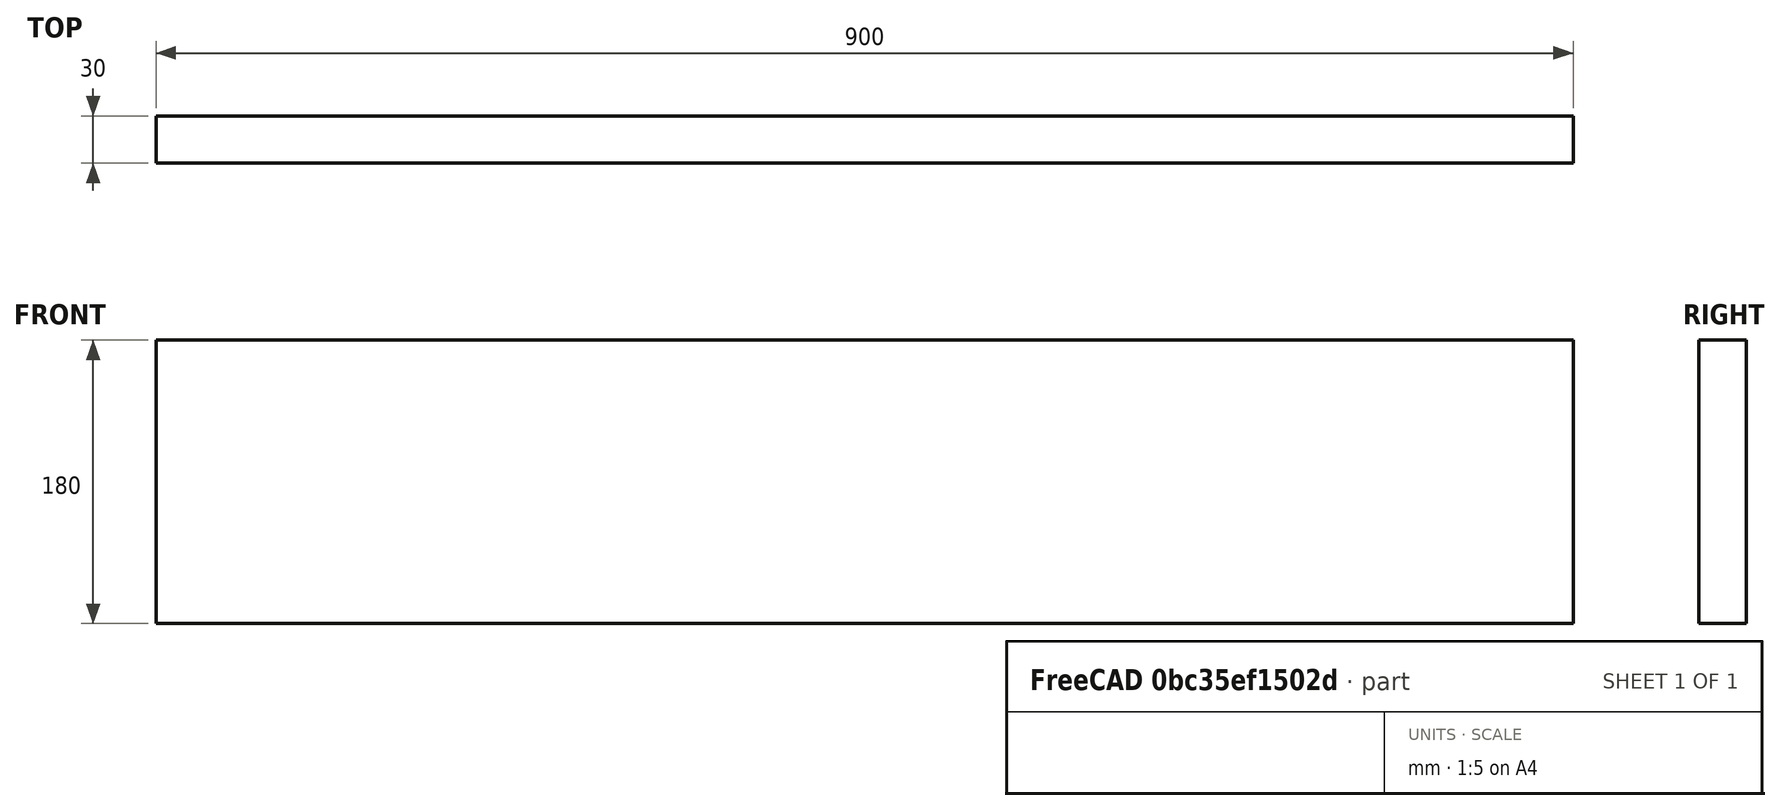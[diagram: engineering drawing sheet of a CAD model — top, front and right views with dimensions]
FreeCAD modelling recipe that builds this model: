
FCSTD DOCUMENT  (FreeCAD 1.0R39319 (Git))
Label: gantry-plate-big
License: All rights reserved
LicenseURL: https://en.wikipedia.org/wiki/All_rights_reserved
objects: Sketcher::SketchObject×1, PartDesign::Pad×1, PartDesign::Body×1
note: 6 computed .brp shape members not serialized (recipe doc carries the construction recipe); baked Part::Feature solids carry a one-line shape summary decoded from their .brp

FEATURE [Sketcher::SketchObject] Sketch
  ArcFitTolerance = 1e-06
  AttachmentSupport = -> [XZ_Plane]
  FullyConstrained = true
  MakeInternals = false
  MapMode = 5
  Placement = pos=(0,0,0) rot=(1,0,0;1.5708rad)
  sketch-geometry (4):
    g0: LineSegment StartX=0 StartY=0 StartZ=0 EndX=900 EndY=0 EndZ=0
    g1: LineSegment StartX=900 StartY=0 StartZ=0 EndX=900 EndY=180 EndZ=0
    g2: LineSegment StartX=900 StartY=180 StartZ=0 EndX=0 EndY=180 EndZ=0
    g3: LineSegment StartX=0 StartY=180 StartZ=0 EndX=0 EndY=0 EndZ=0
  constraints (11):
    c: Coincident(g0,g1)
    c: Coincident(g1,g2)
    c: Coincident(g2,g3)
    c: Coincident(g3,g0)
    c: Horizontal(g0)
    c: Horizontal(g2)
    c: Vertical(g1)
    c: Vertical(g3)
    c: Distance(g1,g3) = 900
    c: Distance(g0,g2) = 180
    c: Coincident(g0,g-1)
FEATURE [PartDesign::Pad] Pad
  Direction = (0,-1,2e-16)
  Length = 30
  Length2 = 10
  Placement = pos=(0,0,0) rot=(1,0,0;1.5708rad)
  Profile = -> Sketch
  ReferenceAxis = -> Sketch [N_Axis]
  Refine = true
  Suppressed = false
  Type = 0
FEATURE [PartDesign::Body] Body
  AllowCompound = false
  Group = -> [Sketch,Pad]
  Origin = -> Origin
  Tip = -> Pad
